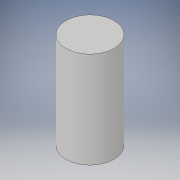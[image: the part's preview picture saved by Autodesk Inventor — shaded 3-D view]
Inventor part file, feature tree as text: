
AUTODESK INVENTOR PART (.ipt)
format: ipt  version: 2019.3 (Build 233278000, 278)  size: 88,064 bytes
history: native  units: mm
features: extrude x1, sketch x1
ambient origin geometry x8: Origin, YZ Plane, XZ Plane, XY Plane, X Axis, Y Axis, Z Axis, Center Point
bodies: Solid1 (feature_tree)
feature tree (2):
  extrude  "Extrusion1"  Depth=20.0mm TaperAngle=0.0deg
  sketch  "Sketch1"  dims[d0=10.0mm d1=20.0mm d2=0.0mm]
